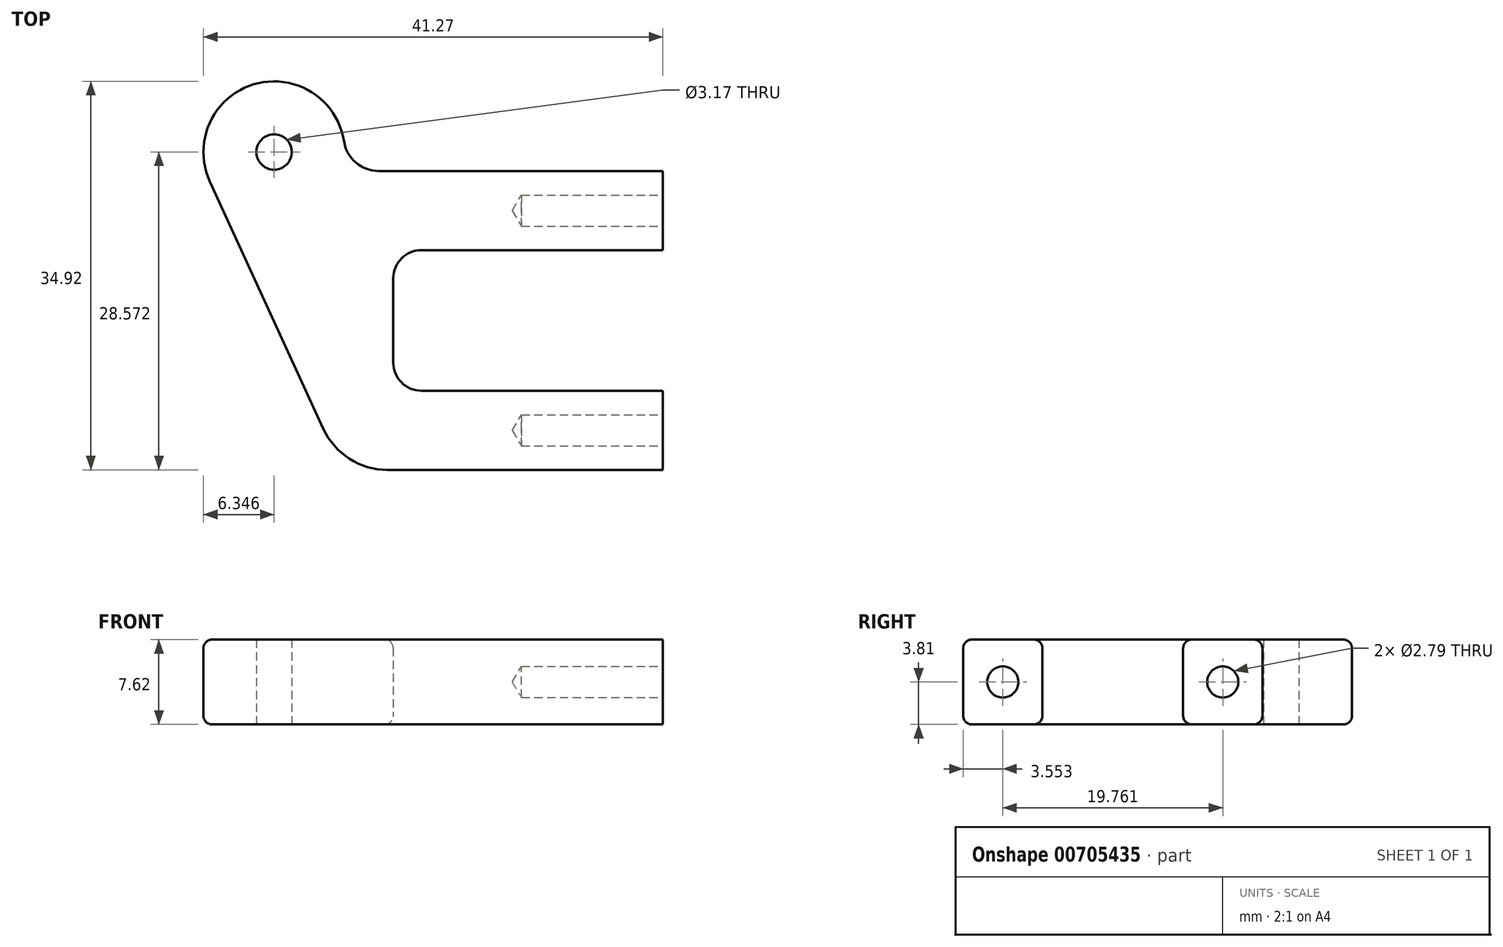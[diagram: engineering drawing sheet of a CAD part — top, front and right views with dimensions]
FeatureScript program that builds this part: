
annotation { "Feature Type Name" : "Feature", "Feature Type Description" : "" }
export const myFeature = defineFeature(function(context is Context, id is Id, definition is map)
    precondition{}
    {
        {
            var Q0;
            Q0=qCreatedBy(makeId("Top.planeOp"),FACE);
            var sketch = newSketch(context, id + "F0", { "sketchPlane" : qUnion([Q0])});
            skLineSegment(sketch, "E0", {"start": v(-34.96, 27.66) * mm, "end": v(-9.45, 27.66) * mm});
            skLineSegment(sketch, "E1", {"start": v(-9.45, 27.66) * mm, "end": v(-9.45, 20.55) * mm});
            skLineSegment(sketch, "E2", {"start": v(-9.45, 20.55) * mm, "end": v(-31.13, 20.55) * mm});
            skLineSegment(sketch, "E3", {"start": v(-33.67, 18) * mm, "end": v(-33.67, 10.44) * mm});
            skLineSegment(sketch, "E4", {"start": v(-31.13, 7.9) * mm, "end": v(-9.45, 7.9) * mm});
            skLineSegment(sketch, "E5", {"start": v(-9.45, 7.9) * mm, "end": v(-9.45, 0.79) * mm});
            skLineSegment(sketch, "E6", {"start": v(-9.45, 0.79) * mm, "end": v(-34.18, 0.79) * mm});
            skLineSegment(sketch, "E7", {"start": v(-39.95, 4.49) * mm, "end": v(-50.15, 26.71) * mm});
            skPoint(sketch, "E8.visualSharp", {"position": v(-33.67, 20.55) * mm});
            skArc(sketch, "E8.filletArc", {"start": v(-31.13, 20.55) * mm, "mid": v(-32.93, 19.8) * mm, "end": v(-33.67, 18) * mm});
            skPoint(sketch, "E9.visualSharp", {"position": v(-33.67, 7.9) * mm});
            skArc(sketch, "E9.filletArc", {"start": v(-33.67, 10.44) * mm, "mid": v(-32.93, 8.64) * mm, "end": v(-31.13, 7.9) * mm});
            skPoint(sketch, "E10.visualSharp", {"position": v(-38.26, 0.79) * mm});
            skArc(sketch, "E10.filletArc", {"start": v(-39.95, 4.49) * mm, "mid": v(-37.61, 1.8) * mm, "end": v(-34.18, 0.79) * mm});
            skPoint(sketch, "E11.visualSharp", {"position": v(-55.63, 38.68) * mm});
            skArc(sketch, "E11.filletArc", {"start": v(-38.1, 30.34) * mm, "mid": v(-46.2, 35.44) * mm, "end": v(-50.15, 26.71) * mm});
            skCircle(sketch, "E12", {"center": v(-44.37, 29.36) * mm, "radius": 1.59 * mm});
            skPoint(sketch, "E13.visualSharp", {"position": v(-38.26, 27.66) * mm});
            skArc(sketch, "E13.filletArc", {"start": v(-38.1, 30.34) * mm, "mid": v(-37.03, 28.42) * mm, "end": v(-34.96, 27.66) * mm});
            skSolve(sketch);
        }
        {
            var Q0;
            Q0=makeQuery(id+"F0.imprint","IMPRINT",FACE,{"disambiguationData":[TD([[makeQuery(id+"F0.imprint","IMPRINT",EDGE,{"derivedFrom":sQuery(id+"F0.wireOp",EDGE,"E0")}),-1.0]])]});
            extrude(context, id + "F1", {"entities" : qUnion([Q0]), "depth" : 7.62 * mm, "offsetDistance" : 25.4 * mm});
        }
        {
            var Q0;
            Q0=makeQuery(id+"F1.opExtrude","SWEPT_FACE",FACE,{"disambiguationData":[OSD([sQuery(id+"F0.wireOp",EDGE,"E1")])]});
            var sketch = newSketch(context, id + "F2", { "sketchPlane" : qUnion([Q0])});
            skCircle(sketch, "E14", {"center": v(24.1, 3.81) * mm, "radius": 1.4 * mm});
            skPoint(sketch, "E14.centerSnap0", {"position": v(20.55, 3.81) * mm});
            skPoint(sketch, "E14.centerSnap1", {"position": v(24.1, 0) * mm});
            skSolve(sketch);
        }
        {
            var Q0;
            Q0=sQuery(id+"F2.wireOp",VERTEX,"E14.center");
            var Q1;
            Q1=makeQuery(id+"F1.opExtrude","SWEPT_BODY",BODY,{"disambiguationData":[OSD([sQuery(id+"F0.wireOp",EDGE,"E0"),sQuery(id+"F0.wireOp",EDGE,"E1"),sQuery(id+"F0.wireOp",EDGE,"E2"),sQuery(id+"F0.wireOp",EDGE,"E3"),sQuery(id+"F0.wireOp",EDGE,"E4"),sQuery(id+"F0.wireOp",EDGE,"E5"),sQuery(id+"F0.wireOp",EDGE,"E6"),sQuery(id+"F0.wireOp",EDGE,"E7"),sQuery(id+"F0.wireOp",EDGE,"E8.filletArc"),sQuery(id+"F0.wireOp",EDGE,"E9.filletArc"),sQuery(id+"F0.wireOp",EDGE,"E10.filletArc"),sQuery(id+"F0.wireOp",EDGE,"E11.filletArc"),sQuery(id+"F0.wireOp",EDGE,"E12"),sQuery(id+"F0.wireOp",EDGE,"E13.filletArc")])]});
            hole(context, id + "F3", {"style" : HoleStyle.SIMPLE, "endStyle" : HoleEndStyle.BLIND, "holeDiameter" : 2.8 * mm, "majorDiameter" : 6.35 * mm, "holeDepth" : 12.7 * mm, "isTappedThrough" : true, "tappedDepth" : 12.7 * mm, "tapClearance" : 3, "startFromSketch" : true, "locations" : qUnion([Q0]), "scope" : qUnion([Q1])});
        }
        {
            var Q0;
            Q0=makeQuery(id+"F1.opExtrude","SWEPT_FACE",FACE,{"disambiguationData":[OSD([sQuery(id+"F0.wireOp",EDGE,"E5")])]});
            var sketch = newSketch(context, id + "F4", { "sketchPlane" : qUnion([Q0])});
            skPoint(sketch, "E15", {"position": v(4.34, 3.81) * mm});
            skPoint(sketch, "E15.positionSnap0", {"position": v(0.79, 3.81) * mm});
            skPoint(sketch, "E15.positionSnap1", {"position": v(4.34, 7.62) * mm});
            skSolve(sketch);
        }
        {
            var Q0;
            Q0=sQuery(id+"F4.wireOp",VERTEX,"E15");
            var Q1;
            Q1=makeQuery(id+"F1.opExtrude","SWEPT_BODY",BODY,{"disambiguationData":[OSD([sQuery(id+"F0.wireOp",EDGE,"E0"),sQuery(id+"F0.wireOp",EDGE,"E1"),sQuery(id+"F0.wireOp",EDGE,"E2"),sQuery(id+"F0.wireOp",EDGE,"E3"),sQuery(id+"F0.wireOp",EDGE,"E4"),sQuery(id+"F0.wireOp",EDGE,"E5"),sQuery(id+"F0.wireOp",EDGE,"E6"),sQuery(id+"F0.wireOp",EDGE,"E7"),sQuery(id+"F0.wireOp",EDGE,"E8.filletArc"),sQuery(id+"F0.wireOp",EDGE,"E9.filletArc"),sQuery(id+"F0.wireOp",EDGE,"E10.filletArc"),sQuery(id+"F0.wireOp",EDGE,"E11.filletArc"),sQuery(id+"F0.wireOp",EDGE,"E12"),sQuery(id+"F0.wireOp",EDGE,"E13.filletArc")])]});
            hole(context, id + "F5", {"style" : HoleStyle.SIMPLE, "endStyle" : HoleEndStyle.BLIND, "holeDiameter" : 2.8 * mm, "majorDiameter" : 6.35 * mm, "holeDepth" : 12.7 * mm, "isTappedThrough" : true, "tappedDepth" : 12.7 * mm, "tapClearance" : 3, "startFromSketch" : true, "locations" : qUnion([Q0]), "scope" : qUnion([Q1])});
        }
        {
            var Q0;
            Q0=makeQuery(id+"F1.opExtrude","CAP_EDGE",EDGE,{"disambiguationData":[OSD([sQuery(id+"F0.wireOp",EDGE,"E0")])],"isStart":false});
            fillet(context, id + "F6", {"entities" : qUnion([Q0]), "radius" : 0.76 * mm, "tangentPropagation" : true, "allowEdgeOverflow" : false});
        }
        {
            var Q0;
            Q0=makeQuery(id+"F1.opExtrude","CAP_EDGE",EDGE,{"disambiguationData":[OSD([sQuery(id+"F0.wireOp",EDGE,"E3")])],"isStart":false});
            fillet(context, id + "F7", {"entities" : qUnion([Q0]), "radius" : 0.76 * mm, "tangentPropagation" : true, "allowEdgeOverflow" : false});
        }
        {
            var Q0;
            Q0=makeQuery(id+"F1.opExtrude","CAP_EDGE",EDGE,{"disambiguationData":[OSD([sQuery(id+"F0.wireOp",EDGE,"E11.filletArc")])],"isStart":true});
            var Q1;
            Q1=makeQuery(id+"F1.opExtrude","CAP_EDGE",EDGE,{"disambiguationData":[OSD([sQuery(id+"F0.wireOp",EDGE,"E3")])],"isStart":true});
            fillet(context, id + "F8", {"entities" : qUnion([Q0, Q1]), "radius" : 0.76 * mm, "tangentPropagation" : true, "allowEdgeOverflow" : false});
        }
    });
